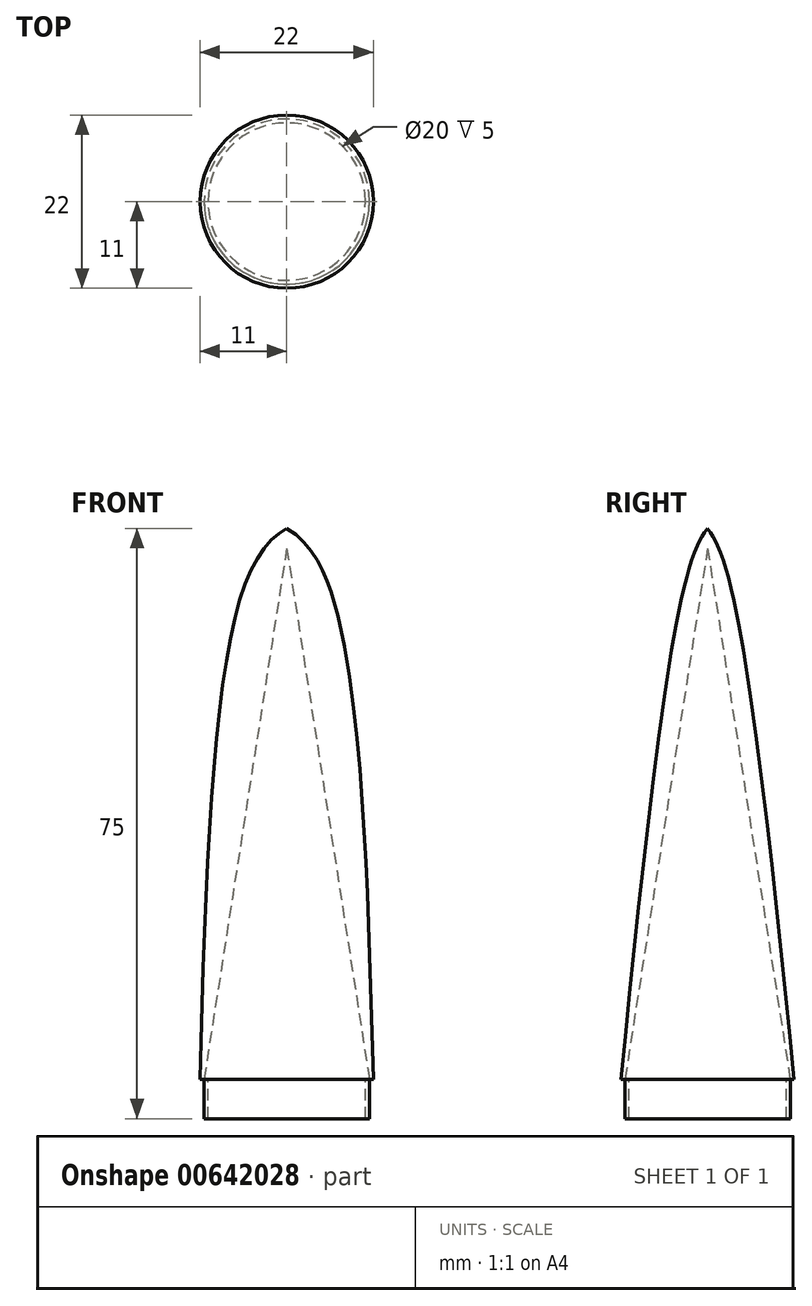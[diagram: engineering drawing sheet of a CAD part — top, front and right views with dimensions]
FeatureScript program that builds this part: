
annotation { "Feature Type Name" : "Feature", "Feature Type Description" : "" }
export const myFeature = defineFeature(function(context is Context, id is Id, definition is map)
    precondition{}
    {
        {
            var Q0;
            Q0=qCreatedBy(makeId("Front.planeOp"),FACE);
            var sketch = newSketch(context, id + "F0", { "sketchPlane" : qUnion([Q0])});
            skLineSegment(sketch, "E0", {"start": v(0, 0) * mm, "end": v(-10.5, 0) * mm});
            skLineSegment(sketch, "E1", {"start": v(-10.5, 0) * mm, "end": v(-10.5, -5) * mm});
            skLineSegment(sketch, "E2", {"start": v(-10.5, 0) * mm, "end": v(-11, 0) * mm});
            skLineSegment(sketch, "E3", {"start": v(0, 0) * mm, "end": v(0, 70) * mm});
            skLineSegment(sketch, "E4", {"start": v(-10.5, -5) * mm, "end": v(0, -5) * mm});
            skFitSpline(sketch, "E5", {"points": [v(0, 70) * mm, v(-5.7, 61.72) * mm, v(-11, 0) * mm], "startDerivative": vector(-23.58, -13.58) * mm, "endDerivative": vector(-2.73, -110.96) * mm});
            skFitSpline(sketch, "E6.MirrorCS", {"points": [v(0, 70) * mm, v(5.7, 61.72) * mm, v(11, 0) * mm], "startDerivative": vector(23.58, -13.58) * mm, "endDerivative": vector(2.73, -110.96) * mm});
            skLineSegment(sketch, "E7.MirrorCS", {"start": v(10.5, 0) * mm, "end": v(11, 0) * mm});
            skLineSegment(sketch, "E8.MirrorCS", {"start": v(0, 0) * mm, "end": v(10.5, 0) * mm});
            skLineSegment(sketch, "E9.MirrorCS", {"start": v(10.5, 0) * mm, "end": v(10.5, -5) * mm});
            skLineSegment(sketch, "E10.MirrorCS", {"start": v(10.5, -5) * mm, "end": v(0, -5) * mm});
            skFitSpline(sketch, "E11", {"points": [v(0, 67.45) * mm, v(-3.8, 61.42) * mm, v(-10.5, 0) * mm], "startDerivative": vector(-15.6, -20.72) * mm, "endDerivative": vector(-6.72, -102.1) * mm});
            skFitSpline(sketch, "E12.MirrorCS", {"points": [v(0, 67.45) * mm, v(3.8, 61.42) * mm, v(10.5, 0) * mm], "startDerivative": vector(15.6, -20.72) * mm, "endDerivative": vector(6.72, -102.1) * mm});
            skSolve(sketch);
        }
        {
            var Q0;
            Q0=qCreatedBy(makeId("Top.planeOp"),FACE);
            var sketch = newSketch(context, id + "F1", { "sketchPlane" : qUnion([Q0])});
            skCircle(sketch, "E13", {"center": v(0, 0) * mm, "radius": 11 * mm});
            skSolve(sketch);
        }
        {
            var Q0;
            Q0=qCreatedBy(makeId("Top.planeOp"),FACE);
            var sketch = newSketch(context, id + "F2", { "sketchPlane" : qUnion([Q0])});
            skCircle(sketch, "E14", {"center": v(0, 0) * mm, "radius": 10.5 * mm});
            skSolve(sketch);
        }
        {
            var Q0;
            Q0=sQuery(id+"F0.wireOp",VERTEX,"E6.MirrorCS.0.internal");
            var Q1;
            Q1=makeQuery(id+"F1.imprint","IMPRINT",FACE,{"disambiguationData":[TD([[makeQuery(id+"F1.imprint","IMPRINT",EDGE,{"derivedFrom":sQuery(id+"F1.wireOp",EDGE,"E13")}),1.0]])]});
            var Q2;
            Q2=sQuery(id+"F0.wireOp",EDGE,"E5");
            var Q3;
            Q3=sQuery(id+"F0.wireOp",EDGE,"E6.MirrorCS");
            loft(context, id + "F3", {"addGuides" : true, "sheetProfilesArray" : [{ "sheetProfileEntities" : qUnion([Q0]) }, { "sheetProfileEntities" : qUnion([Q1]) }], "guidesArray" : [{ "guideEntities" : qUnion([Q2]), "guideDerivativeType" : LoftGuideDerivativeType.DEFAULT, "guideDerivativeMagnitude" : 1 }, { "guideEntities" : qUnion([Q3]), "guideDerivativeType" : LoftGuideDerivativeType.DEFAULT, "guideDerivativeMagnitude" : 1 }]});
        }
        {
            var Q1;
            Q1=sQuery(id+"F0.wireOp",VERTEX,"E12.MirrorCS.0.internal");
            var Q2;
            Q2=makeQuery(id+"F2.imprint","IMPRINT",FACE,{"disambiguationData":[TD([[makeQuery(id+"F2.imprint","IMPRINT",EDGE,{"derivedFrom":sQuery(id+"F2.wireOp",EDGE,"E14")}),1.0]])]});
            loft(context, id + "F4", {"operationType" : NewBodyOperationType.REMOVE, "sheetProfilesArray" : [{ "sheetProfileEntities" : qUnion([Q1]) }, { "sheetProfileEntities" : qUnion([Q2]) }]});
        }
        {
            var Q0;
            Q0=qCreatedBy(makeId("Top.planeOp"),FACE);
            var sketch = newSketch(context, id + "F5", { "sketchPlane" : qUnion([Q0])});
            skCircle(sketch, "E15", {"center": v(0, 0) * mm, "radius": 10.5 * mm});
            skCircle(sketch, "E16", {"center": v(0, 0) * mm, "radius": 10 * mm});
            skSolve(sketch);
        }
        {
            var Q0;
            Q0=makeQuery(id+"F5.imprint","IMPRINT",FACE,{"disambiguationData":[TD([[makeQuery(id+"F5.imprint","IMPRINT",EDGE,{"derivedFrom":sQuery(id+"F5.wireOp",EDGE,"E15")}),1.0]])]});
            extrude(context, id + "F6", {"entities" : qUnion([Q0]), "operationType" : NewBodyOperationType.ADD, "oppositeDirection" : true, "depth" : 5 * mm, "offsetDistance" : 25 * mm});
        }
    });
